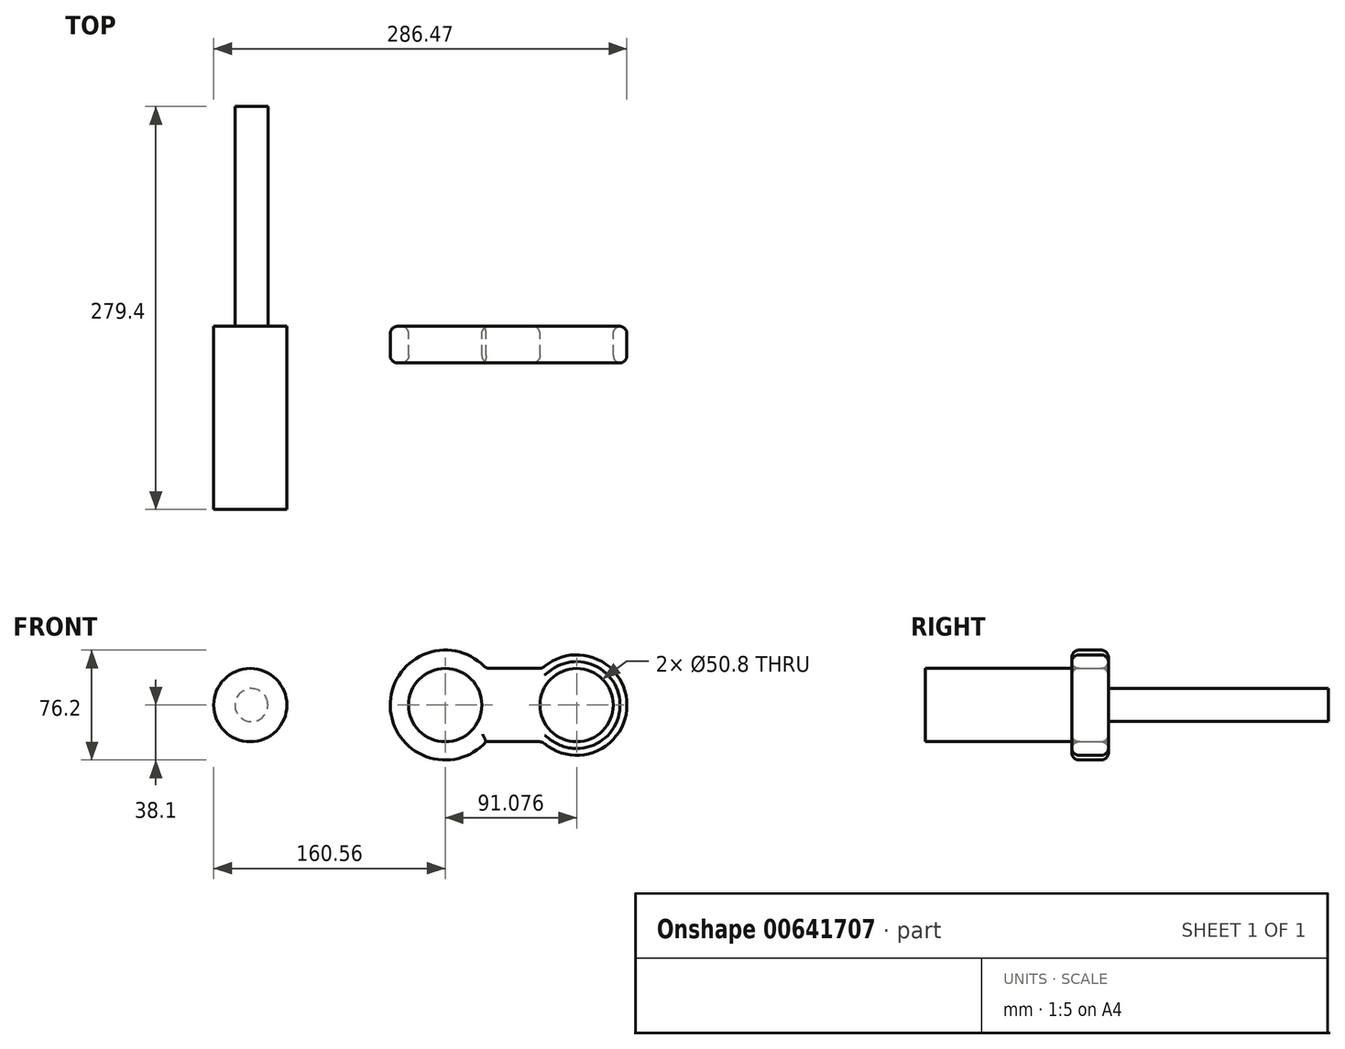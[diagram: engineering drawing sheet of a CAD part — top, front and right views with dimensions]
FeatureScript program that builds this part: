
annotation { "Feature Type Name" : "Feature", "Feature Type Description" : "" }
export const myFeature = defineFeature(function(context is Context, id is Id, definition is map)
    precondition{}
    {
        {
            var Q0;
            Q0=qCreatedBy(makeId("Front.planeOp"),FACE);
            var sketch = newSketch(context, id + "F0", { "sketchPlane" : qUnion([Q0])});
            skCircle(sketch, "E0", {"center": v(0, 0) * mm, "radius": 38.1 * mm});
            skCircle(sketch, "E1", {"center": v(91.08, 0) * mm, "radius": 34.84 * mm});
            skCircle(sketch, "E2", {"center": v(0, 0) * mm, "radius": 25.4 * mm});
            skCircle(sketch, "E3", {"center": v(91.08, 0) * mm, "radius": 25.4 * mm});
            skLineSegment(sketch, "E4", {"start": v(0, 0) * mm, "end": v(91.08, 0) * mm, "construction": true});
            skLineSegment(sketch, "E5", {"start": v(28.36, 25.45) * mm, "end": v(67.28, 25.45) * mm});
            skLineSegment(sketch, "E6.MirrorCS", {"start": v(28.36, -25.45) * mm, "end": v(67.28, -25.45) * mm});
            skSolve(sketch);
        }
        {
            var Q0;
            Q0=makeQuery(id+"F0.imprint","IMPRINT",FACE,{"disambiguationData":[TD([[makeQuery(id+"F0.imprint","IMPRINT",EDGE,{"derivedFrom":sQuery(id+"F0.wireOp",EDGE,"E2")}),-1.0]])]});
            var Q1;
            {var subQ0=sQuery(id+"F0.wireOp",EDGE,"E5");Q1=makeQuery(id+"F0.imprint","IMPRINT",FACE,{"disambiguationData":[TD([[makeQuery(id+"F0.imprint","IMPRINT",EDGE,{"derivedFrom":subQ0}),-1.0]])]});}
            var Q2;
            Q2=makeQuery(id+"F0.imprint","IMPRINT",FACE,{"disambiguationData":[TD([[makeQuery(id+"F0.imprint","IMPRINT",EDGE,{"derivedFrom":sQuery(id+"F0.wireOp",EDGE,"E3")}),-1.0]])]});
            extrude(context, id + "F1", {"entities" : qUnion([Q0, Q1, Q2]), "depth" : 25.4 * mm, "offsetDistance" : 25.4 * mm});
        }
        {
            var Q0;
            Q0=makeQuery(id+"F1.opExtrude","SWEPT_EDGE",EDGE,{"disambiguationData":[OSD([sQuery(id+"F0.wireOp",EDGE,"E0"),sQuery(id+"F0.wireOp",EDGE,"E5")])]});
            var Q1;
            Q1=makeQuery(id+"F1.opExtrude","SWEPT_EDGE",EDGE,{"disambiguationData":[OSD([sQuery(id+"F0.wireOp",EDGE,"E1"),sQuery(id+"F0.wireOp",EDGE,"E5")])]});
            var Q2;
            Q2=makeQuery(id+"F1.opExtrude","CAP_EDGE",EDGE,{"disambiguationData":[OSD([sQuery(id+"F0.wireOp",EDGE,"E6.MirrorCS")])],"isStart":false});
            var Q3;
            Q3=makeQuery(id+"F1.opExtrude","CAP_EDGE",EDGE,{"disambiguationData":[OSD([sQuery(id+"F0.wireOp",EDGE,"E0")])],"isStart":false});
            var Q4;
            Q4=makeQuery(id+"F1.opExtrude","SWEPT_EDGE",EDGE,{"disambiguationData":[OSD([sQuery(id+"F0.wireOp",EDGE,"E1"),sQuery(id+"F0.wireOp",EDGE,"E6.MirrorCS")])]});
            var Q5;
            Q5=makeQuery(id+"F1.opExtrude","CAP_EDGE",EDGE,{"disambiguationData":[OSD([sQuery(id+"F0.wireOp",EDGE,"E6.MirrorCS")])],"isStart":true});
            var Q6;
            Q6=makeQuery(id+"F1.opExtrude","CAP_EDGE",EDGE,{"disambiguationData":[OSD([sQuery(id+"F0.wireOp",EDGE,"E1")])],"isStart":true});
            var Q7;
            Q7=makeQuery(id+"F1.opExtrude","CAP_EDGE",EDGE,{"disambiguationData":[OSD([sQuery(id+"F0.wireOp",EDGE,"E1")])],"isStart":false});
            var Q8;
            Q8=makeQuery(id+"F1.opExtrude","CAP_EDGE",EDGE,{"disambiguationData":[OSD([sQuery(id+"F0.wireOp",EDGE,"E3")])],"isStart":false});
            var Q9;
            Q9=makeQuery(id+"F1.opExtrude","CAP_EDGE",EDGE,{"disambiguationData":[OSD([sQuery(id+"F0.wireOp",EDGE,"E0")])],"isStart":true});
            var Q10;
            Q10=makeQuery(id+"F1.opExtrude","CAP_EDGE",EDGE,{"disambiguationData":[OSD([sQuery(id+"F0.wireOp",EDGE,"E2")])],"isStart":true});
            var Q11;
            Q11=makeQuery(id+"F1.opExtrude","CAP_EDGE",EDGE,{"disambiguationData":[OSD([sQuery(id+"F0.wireOp",EDGE,"E2")])],"isStart":false});
            var Q12;
            Q12=makeQuery(id+"F1.opExtrude","CAP_EDGE",EDGE,{"disambiguationData":[OSD([sQuery(id+"F0.wireOp",EDGE,"E5")])],"isStart":false});
            var Q13;
            Q13=makeQuery(id+"F1.opExtrude","CAP_FACE",FACE,{"disambiguationData":[OSD([sQuery(id+"F0.wireOp",EDGE,"E0"),sQuery(id+"F0.wireOp",EDGE,"E1"),sQuery(id+"F0.wireOp",EDGE,"E2"),sQuery(id+"F0.wireOp",EDGE,"E3"),sQuery(id+"F0.wireOp",EDGE,"E5"),sQuery(id+"F0.wireOp",EDGE,"E6.MirrorCS")])],"isStart":true});
            var Q14;
            Q14=makeQuery(id+"F1.opExtrude","CAP_FACE",FACE,{"disambiguationData":[OSD([sQuery(id+"F0.wireOp",EDGE,"E0"),sQuery(id+"F0.wireOp",EDGE,"E1"),sQuery(id+"F0.wireOp",EDGE,"E2"),sQuery(id+"F0.wireOp",EDGE,"E3"),sQuery(id+"F0.wireOp",EDGE,"E5"),sQuery(id+"F0.wireOp",EDGE,"E6.MirrorCS")])],"isStart":false});
            fillet(context, id + "F2", {"entities" : qUnion([Q0, Q1, Q2, Q3, Q4, Q5, Q6, Q7, Q8, Q9, Q10, Q11, Q12, Q13, Q14]), "radius" : 5.08 * mm, "tangentPropagation" : true, "allowEdgeOverflow" : false});
        }
        {
            var Q0;
            Q0=qCreatedBy(makeId("Front.planeOp"),FACE);
            var sketch = newSketch(context, id + "F3", { "sketchPlane" : qUnion([Q0])});
            skCircle(sketch, "E7", {"center": v(-44.01, 0) * mm, "radius": 12.7 * mm});
            skCircle(sketch, "E8", {"center": v(-135.16, 0) * mm, "radius": 25.4 * mm});
            skSolve(sketch);
        }
        {
            var Q0;
            Q0=makeQuery(id+"F3.imprint","IMPRINT",FACE,{"disambiguationData":[TD([[makeQuery(id+"F3.imprint","IMPRINT",EDGE,{"derivedFrom":sQuery(id+"F3.wireOp",EDGE,"E8")}),1.0]])]});
            extrude(context, id + "F4", {"entities" : qUnion([Q0]), "depth" : 127 * mm, "offsetDistance" : 25.4 * mm});
        }
        {
            var Q0;
            Q0=qCreatedBy(makeId("Front.planeOp"),FACE);
            var sketch = newSketch(context, id + "F5", { "sketchPlane" : qUnion([Q0])});
            skCircle(sketch, "E9", {"center": v(-134.35, 0) * mm, "radius": 11.43 * mm});
            skSolve(sketch);
        }
        {
            var Q0;
            Q0 = qSketchRegion(id + "F5", true);
            extrude(context, id + "F6", {"entities" : qUnion([Q0]), "operationType" : NewBodyOperationType.ADD, "oppositeDirection" : true, "depth" : 152.4 * mm, "offsetDistance" : 25.4 * mm});
        }
    });
